# Revit family: 120375_CCL-UB-With_Shelf_Angles
name_source: partatom
category: Structural Framing
revit_build: Autodesk Revit 2013 (Build: 20121003_2115(x64)
units: mm (PartAtom-declared; Revit-internal decimal feet)

## types (35) — shared parameters
Angle Type = RSA-Rectangular Steel Angle : 200x150x18RSA
Type Comments = Steel 43-275

## per-type parameters (varying)
| type | A | W | bf | d | k | kr | tf | tw |
| UB305x127x37 | 0.01 m² | 0.037 | 124 mm | 304 mm | 20 mm  [stored 0.0656168 ft] | 9 mm  [stored 0.0295276 ft] | 11 mm | 7 mm |
| UB406x178x67 | 0.01 m² | 0.0671 | 179 mm | 409 mm | 25 mm  [stored 0.082021 ft] | 10 mm  [stored 0.0328084 ft] | 14 mm  [stored 0.0459318 ft] | 9 mm  [stored 0.0295276 ft] |
| UB457x191x98 | 0.01 m² | 0.0983 | 193 mm | 467 mm | 30 mm  [stored 0.0984252 ft] | 10 mm  [stored 0.0328084 ft] | 20 mm  [stored 0.0656168 ft] | 11 mm |
| UB686x254x170 | 0.02 m² | 0.1702 | 256 mm | 693 mm | 39 mm | 15 mm  [stored 0.0492126 ft] | 24 mm | 15 mm  [stored 0.0492126 ft] |
| UB1016x305x487 | 0.06 m² | 0.4866 | 309 mm | 1036 mm | 84 mm | 30 mm  [stored 0.0984252 ft] | 54 mm | 30 mm  [stored 0.0984252 ft] |
| UB356x171x57 | 0.01 m² | 0.057 | 172 mm | 359 mm | 23 mm | 10 mm  [stored 0.0328084 ft] | 13 mm | 8 mm  [stored 0.0262467 ft] |
| UB762x267x147 | 0.02 m² | 0.1469 | 265 mm | 754 mm | 34 mm | 17 mm | 18 mm  [stored 0.0590551 ft] | 13 mm |
| UB254x146x43 | 0.01 m² | 0.043 | 147 mm | 260 mm | 20 mm  [stored 0.0656168 ft] | 8 mm  [stored 0.0262467 ft] | 13 mm | 7 mm |
| UB838x292x194 | 0.02 m² | 0.1938 | 292 mm | 841 mm | 40 mm | 18 mm  [stored 0.0590551 ft] | 22 mm | 15 mm  [stored 0.0492126 ft] |
| UB457x152x60 | 0.01 m² | 0.0598 | 153 mm | 455 mm | 24 mm | 10 mm  [stored 0.0328084 ft] | 13 mm | 8 mm  [stored 0.0262467 ft] |
| UB406x140x46 | 0.01 m² | 0.046 | 142 mm | 402 mm | 21 mm | 10 mm  [stored 0.0328084 ft] | 11 mm | 7 mm |
| UB762x267x173 | 0.02 m² | 0.173 | 267 mm | 762 mm | 38 mm | 17 mm | 22 mm | 14 mm  [stored 0.0459318 ft] |
| UB457x152x52 | 0.01 m² | 0.0523 | 152 mm | 450 mm | 21 mm | 10 mm  [stored 0.0328084 ft] | 11 mm | 8 mm  [stored 0.0262467 ft] |
| UB356x127x33 | 0 m² | 0.0331 | 125 mm | 349 mm | 19 mm | 10 mm  [stored 0.0328084 ft] | 9 mm  [stored 0.0295276 ft] | 6 mm  [stored 0.019685 ft] |
| UB838x292x176 | 0.02 m² | 0.1759 | 292 mm | 835 mm | 37 mm | 18 mm  [stored 0.0590551 ft] | 19 mm | 14 mm  [stored 0.0459318 ft] |
| UB406x178x54 | 0.01 m² | 0.0541 | 178 mm | 403 mm | 21 mm | 10 mm  [stored 0.0328084 ft] | 11 mm | 8 mm  [stored 0.0262467 ft] |
| UB356x171x51 | 0.01 m² | 0.051 | 172 mm | 356 mm | 22 mm | 10 mm  [stored 0.0328084 ft] | 12 mm  [stored 0.0393701 ft] | 7 mm |
| UB610x229x113 | 0.01 m² | 0.113 | 228 mm | 607 mm | 30 mm  [stored 0.0984252 ft] | 13 mm | 17 mm | 11 mm |
| UB356x171x45 | 0.01 m² | 0.045 | 171 mm | 352 mm | 20 mm  [stored 0.0656168 ft] | 10 mm  [stored 0.0328084 ft] | 10 mm  [stored 0.0328084 ft] | 7 mm |
| UB457x191x74 | 0.01 m² | 0.0743 | 191 mm | 457 mm | 25 mm  [stored 0.082021 ft] | 10 mm  [stored 0.0328084 ft] | 15 mm  [stored 0.0492126 ft] | 9 mm  [stored 0.0295276 ft] |
| UB406x178x60 | 0.01 m² | 0.0601 | 178 mm | 406 mm | 23 mm | 10 mm  [stored 0.0328084 ft] | 13 mm | 8 mm  [stored 0.0262467 ft] |
| UB203x133x25 | 0 m² | 0.0251 | 133 mm | 203 mm | 15 mm  [stored 0.0492126 ft] | 8 mm  [stored 0.0262467 ft] | 8 mm  [stored 0.0262467 ft] | 6 mm  [stored 0.019685 ft] |
| UB533x210x82 | 0.01 m² | 0.0822 | 209 mm | 528 mm | 26 mm | 13 mm | 13 mm | 10 mm  [stored 0.0328084 ft] |
| UB762x267x134 | 0.02 m² | 0.1339 | 264 mm | 750 mm | 32 mm | 17 mm | 16 mm  [stored 0.0524934 ft] | 12 mm  [stored 0.0393701 ft] |
| UB406x140x39 | 0 m² | 0.039 | 142 mm | 397 mm | 19 mm | 10 mm  [stored 0.0328084 ft] | 9 mm  [stored 0.0295276 ft] | 6 mm  [stored 0.019685 ft] |
| UB610x229x101 | 0.01 m² | 0.1012 | 228 mm | 602 mm | 28 mm | 13 mm | 15 mm  [stored 0.0492126 ft] | 11 mm |
| UB533x210x92 | 0.01 m² | 0.0921 | 209 mm | 533 mm | 28 mm | 13 mm | 16 mm  [stored 0.0524934 ft] | 10 mm  [stored 0.0328084 ft] |
| UB178x102x19 | 0 m² | 0.019 | 102 mm | 178 mm | 16 mm  [stored 0.0524934 ft] | 8 mm  [stored 0.0262467 ft] | 8 mm  [stored 0.0262467 ft] | 5 mm  [stored 0.0164042 ft] |
| UB533x210x101 | 0.01 m² | 0.101 | 210 mm | 537 mm | 30 mm  [stored 0.0984252 ft] | 13 mm | 17 mm | 11 mm |
| UB203x133x30 | 0 m² | 0.03 | 134 mm | 207 mm | 17 mm | 8 mm  [stored 0.0262467 ft] | 10 mm  [stored 0.0328084 ft] | 6 mm  [stored 0.019685 ft] |
| UB254x146x31 | 0 m² | 0.0311 | 146 mm | 252 mm | 16 mm  [stored 0.0524934 ft] | 8 mm  [stored 0.0262467 ft] | 9 mm  [stored 0.0295276 ft] | 6 mm  [stored 0.019685 ft] |
| UB305x165x40 | 0.01 m² | 0.0403 | 165 mm | 304 mm | 19 mm | 9 mm  [stored 0.0295276 ft] | 10 mm  [stored 0.0328084 ft] | 6 mm  [stored 0.019685 ft] |
| UB457x191x67 | 0.01 m² | 0.0671 | 190 mm | 454 mm | 23 mm | 10 mm  [stored 0.0328084 ft] | 13 mm | 9 mm  [stored 0.0295276 ft] |
| UB686x254x125 WITH SHELF ANGLES | 0.02 m² | 0.1252 | 253 mm | 678 mm | 31 mm | 15 mm  [stored 0.0492126 ft] | 16 mm  [stored 0.0524934 ft] | 12 mm  [stored 0.0393701 ft] |
| UB762x267x173 WITH SHELF ANGLES | 0.02 m² | 0.173 | 267 mm | 762 mm | 38 mm | 17 mm | 22 mm | 14 mm  [stored 0.0459318 ft] |

note: [stored X ft] marks values corroborated as IEEE doubles in the binary element streams (Revit-internal decimal feet)

## geometry (parser evidence)
native form markers: Sweep x5
no freeform markers — native parametric forms only
